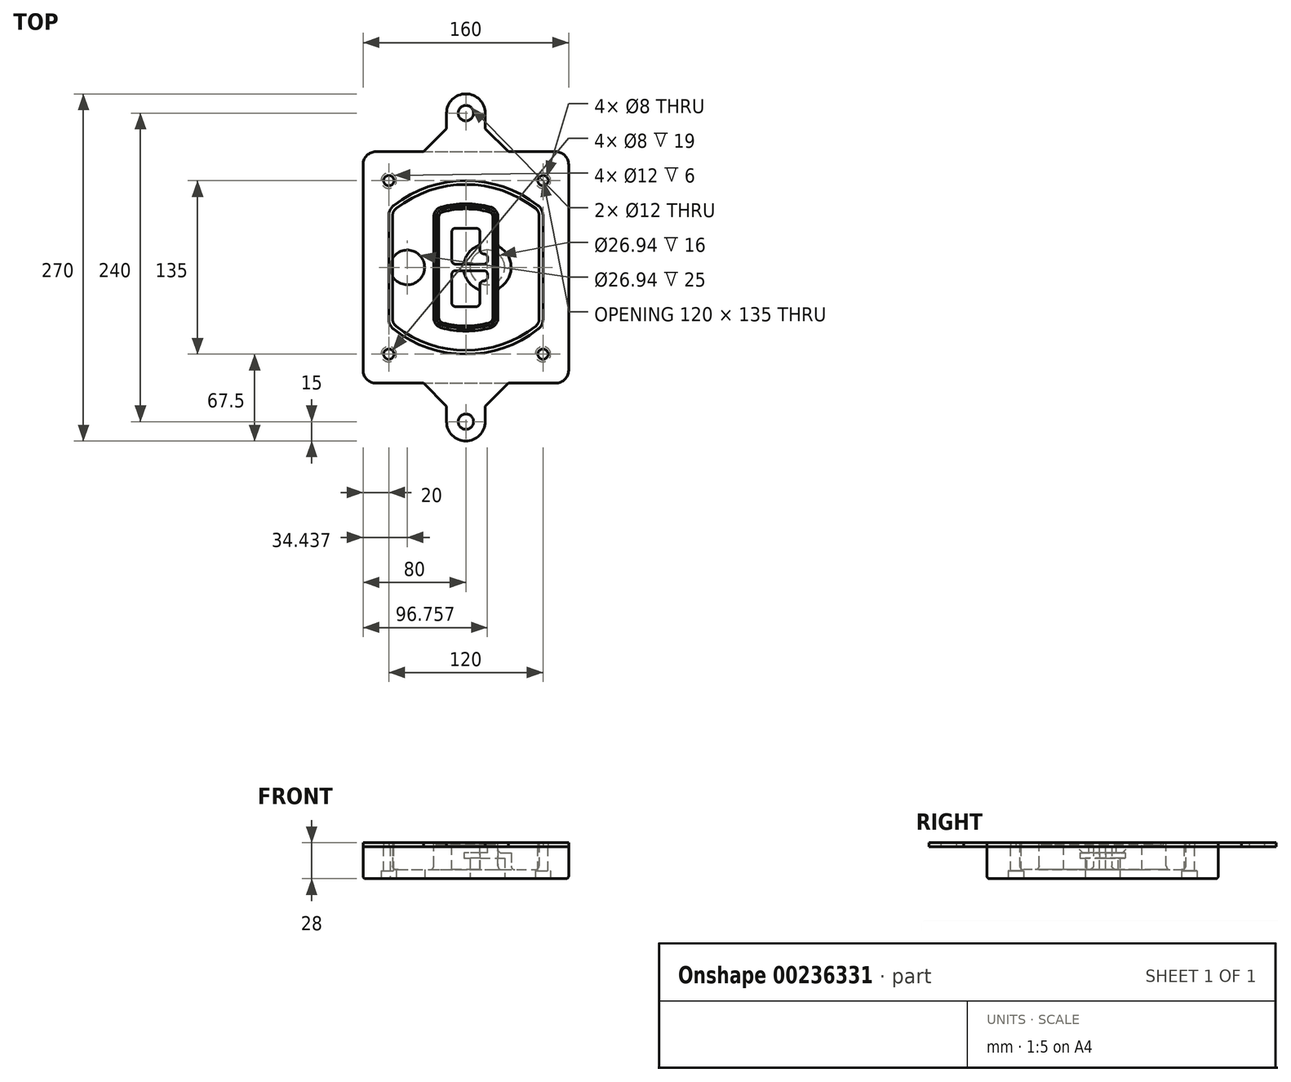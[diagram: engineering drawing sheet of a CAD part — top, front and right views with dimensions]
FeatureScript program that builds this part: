
annotation { "Feature Type Name" : "Feature", "Feature Type Description" : "" }
export const myFeature = defineFeature(function(context is Context, id is Id, definition is map)
    precondition{}
    {
        {
            var Q0;
            Q0=qCreatedBy(makeId("Top.planeOp"),FACE);
            var sketch = newSketch(context, id + "F0", { "sketchPlane" : qUnion([Q0])});
            skPoint(sketch, "E0.rect.middle", {"position": v(0, 0) * mm});
            skLineSegment(sketch, "E1.bottom", {"start": v(-70, -90) * mm, "end": v(70, -90) * mm});
            skLineSegment(sketch, "E1.top", {"start": v(-70, 90) * mm, "end": v(70, 90) * mm});
            skLineSegment(sketch, "E1.left", {"start": v(-80, -80) * mm, "end": v(-80, 80) * mm});
            skLineSegment(sketch, "E1.right", {"start": v(80, -80) * mm, "end": v(80, 80) * mm});
            skLineSegment(sketch, "E2", {"start": v(-80, 90) * mm, "end": v(80, -90) * mm, "construction": true});
            skLineSegment(sketch, "E3", {"start": v(80, 90) * mm, "end": v(-80, -90) * mm, "construction": true});
            skCircle(sketch, "E4", {"center": v(-60, 67.5) * mm, "radius": 4 * mm});
            skCircle(sketch, "E5", {"center": v(60, 67.5) * mm, "radius": 4 * mm});
            skCircle(sketch, "E6", {"center": v(60, -67.5) * mm, "radius": 4 * mm});
            skCircle(sketch, "E7", {"center": v(-60, -67.5) * mm, "radius": 4 * mm});
            skLineSegment(sketch, "E8", {"start": v(-60, 67.5) * mm, "end": v(60, 67.5) * mm, "construction": true});
            skLineSegment(sketch, "E9", {"start": v(60, 67.5) * mm, "end": v(60, -67.5) * mm, "construction": true});
            skLineSegment(sketch, "E10", {"start": v(60, -67.5) * mm, "end": v(-60, -67.5) * mm, "construction": true});
            skLineSegment(sketch, "E11", {"start": v(-60, -67.5) * mm, "end": v(-60, 67.5) * mm, "construction": true});
            skLineSegment(sketch, "E12", {"start": v(-60, 40.3) * mm, "end": v(-60, -40.3) * mm});
            skLineSegment(sketch, "E13", {"start": v(60, 40.3) * mm, "end": v(60, -40.3) * mm});
            skArc(sketch, "E14", {"start": v(56.15, 48.18) * mm, "mid": v(0, 67.5) * mm, "end": v(-56.15, 48.18) * mm});
            skArc(sketch, "E15", {"start": v(-56.15, -48.18) * mm, "mid": v(0, -67.5) * mm, "end": v(56.15, -48.18) * mm});
            skLineSegment(sketch, "E16", {"start": v(-60, 0) * mm, "end": v(60, 0) * mm, "construction": true});
            skPoint(sketch, "E17.visualSharp", {"position": v(-60, -45) * mm});
            skArc(sketch, "E17.filletArc", {"start": v(-60, -40.3) * mm, "mid": v(-58.99, -44.68) * mm, "end": v(-56.15, -48.18) * mm});
            skPoint(sketch, "E18.visualSharp", {"position": v(-60, 45) * mm});
            skArc(sketch, "E18.filletArc", {"start": v(-56.15, 48.18) * mm, "mid": v(-58.99, 44.68) * mm, "end": v(-60, 40.3) * mm});
            skPoint(sketch, "E19.visualSharp", {"position": v(60, 45) * mm});
            skArc(sketch, "E19.filletArc", {"start": v(60, 40.3) * mm, "mid": v(58.99, 44.68) * mm, "end": v(56.15, 48.18) * mm});
            skPoint(sketch, "E20.visualSharp", {"position": v(60, -45) * mm});
            skArc(sketch, "E20.filletArc", {"start": v(56.15, -48.18) * mm, "mid": v(58.99, -44.68) * mm, "end": v(60, -40.3) * mm});
            skPoint(sketch, "E21.visualSharp", {"position": v(-80, 90) * mm});
            skArc(sketch, "E21.filletArc", {"start": v(-70, 90) * mm, "mid": v(-77.07, 87.07) * mm, "end": v(-80, 80) * mm});
            skPoint(sketch, "E22.visualSharp", {"position": v(80, 90) * mm});
            skArc(sketch, "E22.filletArc", {"start": v(80, 80) * mm, "mid": v(77.07, 87.07) * mm, "end": v(70, 90) * mm});
            skPoint(sketch, "E23.visualSharp", {"position": v(80, -90) * mm});
            skArc(sketch, "E23.filletArc", {"start": v(70, -90) * mm, "mid": v(77.07, -87.07) * mm, "end": v(80, -80) * mm});
            skPoint(sketch, "E24.visualSharp", {"position": v(-80, -90) * mm});
            skArc(sketch, "E24.filletArc", {"start": v(-80, -80) * mm, "mid": v(-77.07, -87.07) * mm, "end": v(-70, -90) * mm});
            skArc(sketch, "E25.0", {"start": v(57, 40.3) * mm, "mid": v(56.3, 43.36) * mm, "end": v(54.3, 45.81) * mm});
            skLineSegment(sketch, "E25.1", {"start": v(57, 40.3) * mm, "end": v(57, -40.3) * mm});
            skArc(sketch, "E25.2", {"start": v(54.3, -45.81) * mm, "mid": v(56.3, -43.36) * mm, "end": v(57, -40.3) * mm});
            skArc(sketch, "E25.3", {"start": v(-54.3, -45.81) * mm, "mid": v(0, -64.5) * mm, "end": v(54.3, -45.81) * mm});
            skArc(sketch, "E25.4", {"start": v(-57, -40.3) * mm, "mid": v(-56.3, -43.36) * mm, "end": v(-54.3, -45.81) * mm});
            skArc(sketch, "E25.5", {"start": v(54.3, 45.81) * mm, "mid": v(0, 64.5) * mm, "end": v(-54.3, 45.81) * mm});
            skLineSegment(sketch, "E25.6", {"start": v(-57, 40.3) * mm, "end": v(-57, -40.3) * mm});
            skArc(sketch, "E25.7", {"start": v(-54.3, 45.81) * mm, "mid": v(-56.3, 43.36) * mm, "end": v(-57, 40.3) * mm});
            skArc(sketch, "E26.0", {"start": v(-58.62, 51.33) * mm, "mid": v(-62.58, 46.43) * mm, "end": v(-64, 40.3) * mm});
            skArc(sketch, "E26.1", {"start": v(58.62, 51.33) * mm, "mid": v(0, 71.5) * mm, "end": v(-58.62, 51.33) * mm});
            skArc(sketch, "E26.2", {"start": v(64, 40.3) * mm, "mid": v(62.58, 46.43) * mm, "end": v(58.62, 51.33) * mm});
            skLineSegment(sketch, "E26.3", {"start": v(64, 40.3) * mm, "end": v(64, -40.3) * mm});
            skArc(sketch, "E26.4", {"start": v(58.62, -51.33) * mm, "mid": v(62.58, -46.43) * mm, "end": v(64, -40.3) * mm});
            skLineSegment(sketch, "E26.5", {"start": v(-64, 40.3) * mm, "end": v(-64, -40.3) * mm});
            skArc(sketch, "E26.6", {"start": v(-58.62, -51.33) * mm, "mid": v(0, -71.5) * mm, "end": v(58.62, -51.33) * mm});
            skArc(sketch, "E26.7", {"start": v(-64, -40.3) * mm, "mid": v(-62.58, -46.43) * mm, "end": v(-58.62, -51.33) * mm});
            skSolve(sketch);
        }
        {
            var Q0;
            Q0=makeQuery(id+"F0.imprint","IMPRINT",FACE,{"disambiguationData":[TD([[makeQuery(id+"F0.imprint","IMPRINT",EDGE,{"derivedFrom":sQuery(id+"F0.wireOp",EDGE,"E1.bottom")}),1.0]])]});
            var Q1;
            Q1=makeQuery(id+"F0.imprint","IMPRINT",FACE,{"disambiguationData":[TD([[makeQuery(id+"F0.imprint","IMPRINT",EDGE,{"derivedFrom":sQuery(id+"F0.wireOp",EDGE,"E12")}),1.0]])]});
            var Q2;
            Q2=makeQuery(id+"F0.imprint","IMPRINT",FACE,{"disambiguationData":[TD([[makeQuery(id+"F0.imprint","IMPRINT",EDGE,{"derivedFrom":sQuery(id+"F0.wireOp",EDGE,"E25.0")}),1.0]])]});
            var Q3;
            Q3=makeQuery(id+"F0.imprint","IMPRINT",FACE,{"disambiguationData":[TD([[makeQuery(id+"F0.imprint","IMPRINT",EDGE,{"derivedFrom":sQuery(id+"F0.wireOp",EDGE,"E12")}),-1.0]])]});
            extrude(context, id + "F1", {"entities" : qUnion([Q0, Q1, Q2, Q3]), "oppositeDirection" : true, "depth" : 25 * mm});
        }
        {
            var Q0;
            Q0=makeQuery(id+"F0.imprint","IMPRINT",FACE,{"disambiguationData":[TD([[makeQuery(id+"F0.imprint","IMPRINT",EDGE,{"derivedFrom":sQuery(id+"F0.wireOp",EDGE,"E12")}),1.0]])]});
            extrude(context, id + "F2", {"entities" : qUnion([Q0]), "operationType" : NewBodyOperationType.ADD, "depth" : 3 * mm});
        }
        {
            var Q0;
            Q0=makeQuery(id+"F0.imprint","IMPRINT",FACE,{"disambiguationData":[TD([[makeQuery(id+"F0.imprint","IMPRINT",EDGE,{"derivedFrom":sQuery(id+"F0.wireOp",EDGE,"E25.0")}),1.0]])]});
            extrude(context, id + "F3", {"entities" : qUnion([Q0]), "operationType" : NewBodyOperationType.REMOVE, "oppositeDirection" : true, "depth" : 18 * mm});
        }
        {
            var Q0;
            Q0=makeQuery(id+"F2.opExtrude","CAP_FACE",FACE,{"disambiguationData":[OSD([sQuery(id+"F0.wireOp",EDGE,"E12"),sQuery(id+"F0.wireOp",EDGE,"E13"),sQuery(id+"F0.wireOp",EDGE,"E14"),sQuery(id+"F0.wireOp",EDGE,"E15"),sQuery(id+"F0.wireOp",EDGE,"E17.filletArc"),sQuery(id+"F0.wireOp",EDGE,"E18.filletArc"),sQuery(id+"F0.wireOp",EDGE,"E19.filletArc"),sQuery(id+"F0.wireOp",EDGE,"E20.filletArc"),sQuery(id+"F0.wireOp",EDGE,"E25.0"),sQuery(id+"F0.wireOp",EDGE,"E25.1"),sQuery(id+"F0.wireOp",EDGE,"E25.2"),sQuery(id+"F0.wireOp",EDGE,"E25.3"),sQuery(id+"F0.wireOp",EDGE,"E25.4"),sQuery(id+"F0.wireOp",EDGE,"E25.5"),sQuery(id+"F0.wireOp",EDGE,"E25.6"),sQuery(id+"F0.wireOp",EDGE,"E25.7")])],"isStart":false});
            var sketch = newSketch(context, id + "F4", { "sketchPlane" : qUnion([Q0])});
            skArc(sketch, "E27.0", {"start": v(-19.08, -46.97) * mm, "mid": v(0, -49.5) * mm, "end": v(19.08, -46.97) * mm});
            skArc(sketch, "E28.0", {"start": v(19.08, 46.97) * mm, "mid": v(0, 49.5) * mm, "end": v(-19.08, 46.97) * mm});
            skLineSegment(sketch, "E29", {"start": v(-25, 39.25) * mm, "end": v(-25, -39.25) * mm});
            skLineSegment(sketch, "E30", {"start": v(25, 39.25) * mm, "end": v(25, -39.25) * mm});
            skLineSegment(sketch, "E31", {"start": v(-25, 45.1) * mm, "end": v(25, 45.1) * mm, "construction": true});
            skLineSegment(sketch, "E32", {"start": v(-25, -45.1) * mm, "end": v(25, -45.1) * mm, "construction": true});
            skPoint(sketch, "E33.visualSharp", {"position": v(-25, 45.1) * mm});
            skArc(sketch, "E33.filletArc", {"start": v(-19.08, 46.97) * mm, "mid": v(-23.35, 44.11) * mm, "end": v(-25, 39.25) * mm});
            skPoint(sketch, "E34.visualSharp", {"position": v(25, 45.1) * mm});
            skArc(sketch, "E34.filletArc", {"start": v(25, 39.25) * mm, "mid": v(23.35, 44.11) * mm, "end": v(19.08, 46.97) * mm});
            skPoint(sketch, "E35.visualSharp", {"position": v(25, -45.1) * mm});
            skArc(sketch, "E35.filletArc", {"start": v(19.08, -46.97) * mm, "mid": v(23.35, -44.11) * mm, "end": v(25, -39.25) * mm});
            skPoint(sketch, "E36.visualSharp", {"position": v(-25, -45.1) * mm});
            skArc(sketch, "E36.filletArc", {"start": v(-25, -39.25) * mm, "mid": v(-23.35, -44.11) * mm, "end": v(-19.08, -46.97) * mm});
            skArc(sketch, "E37.0", {"start": v(54.3, 45.81) * mm, "mid": v(0, 64.5) * mm, "end": v(-54.3, 45.81) * mm});
            skArc(sketch, "E37.1", {"start": v(-54.3, 45.81) * mm, "mid": v(-56.3, 43.36) * mm, "end": v(-57, 40.3) * mm});
            skLineSegment(sketch, "E37.2", {"start": v(-57, 40.3) * mm, "end": v(-57, -40.3) * mm});
            skArc(sketch, "E37.3", {"start": v(-57, -40.3) * mm, "mid": v(-56.3, -43.36) * mm, "end": v(-54.3, -45.81) * mm});
            skArc(sketch, "E37.4", {"start": v(-54.3, -45.81) * mm, "mid": v(0, -64.5) * mm, "end": v(54.3, -45.81) * mm});
            skArc(sketch, "E37.5", {"start": v(54.3, -45.81) * mm, "mid": v(56.3, -43.36) * mm, "end": v(57, -40.3) * mm});
            skLineSegment(sketch, "E37.6", {"start": v(57, 40.3) * mm, "end": v(57, -40.3) * mm});
            skArc(sketch, "E37.7", {"start": v(57, 40.3) * mm, "mid": v(56.3, 43.36) * mm, "end": v(54.3, 45.81) * mm});
            skLineSegment(sketch, "E38.0", {"start": v(23, 39.25) * mm, "end": v(23, -39.25) * mm});
            skArc(sketch, "E38.1", {"start": v(18.56, -45.04) * mm, "mid": v(21.76, -42.9) * mm, "end": v(23, -39.25) * mm});
            skArc(sketch, "E38.2", {"start": v(-18.56, -45.04) * mm, "mid": v(0, -47.5) * mm, "end": v(18.56, -45.04) * mm});
            skArc(sketch, "E38.3", {"start": v(-23, -39.25) * mm, "mid": v(-21.76, -42.9) * mm, "end": v(-18.56, -45.04) * mm});
            skLineSegment(sketch, "E38.4", {"start": v(-23, 39.25) * mm, "end": v(-23, -39.25) * mm});
            skArc(sketch, "E38.5", {"start": v(23, 39.25) * mm, "mid": v(21.76, 42.9) * mm, "end": v(18.56, 45.04) * mm});
            skArc(sketch, "E38.6", {"start": v(-18.56, 45.04) * mm, "mid": v(-21.76, 42.9) * mm, "end": v(-23, 39.25) * mm});
            skArc(sketch, "E38.7", {"start": v(18.56, 45.04) * mm, "mid": v(0, 47.5) * mm, "end": v(-18.56, 45.04) * mm});
            skArc(sketch, "E39.0", {"start": v(21, 39.25) * mm, "mid": v(20.18, 41.68) * mm, "end": v(18.04, 43.1) * mm});
            skLineSegment(sketch, "E39.1", {"start": v(21, 39.25) * mm, "end": v(21, -39.25) * mm});
            skArc(sketch, "E39.2", {"start": v(18.04, -43.1) * mm, "mid": v(20.18, -41.68) * mm, "end": v(21, -39.25) * mm});
            skArc(sketch, "E39.3", {"start": v(-18.04, -43.1) * mm, "mid": v(0, -45.5) * mm, "end": v(18.04, -43.1) * mm});
            skArc(sketch, "E39.4", {"start": v(-21, -39.25) * mm, "mid": v(-20.18, -41.68) * mm, "end": v(-18.04, -43.1) * mm});
            skArc(sketch, "E39.5", {"start": v(18.04, 43.1) * mm, "mid": v(0, 45.5) * mm, "end": v(-18.04, 43.1) * mm});
            skLineSegment(sketch, "E39.6", {"start": v(-21, 39.25) * mm, "end": v(-21, -39.25) * mm});
            skArc(sketch, "E39.7", {"start": v(-18.04, 43.1) * mm, "mid": v(-20.18, 41.68) * mm, "end": v(-21, 39.25) * mm});
            skLineSegment(sketch, "E40", {"start": v(-25, 0) * mm, "end": v(25, 0) * mm, "construction": true});
            skLineSegment(sketch, "E41", {"start": v(-11, 5.5) * mm, "end": v(-11, 27.5) * mm});
            skLineSegment(sketch, "E42", {"start": v(-8, 30.5) * mm, "end": v(8, 30.5) * mm});
            skLineSegment(sketch, "E43", {"start": v(11, 27.5) * mm, "end": v(11, 13.5) * mm});
            skLineSegment(sketch, "E44", {"start": v(14, 10.5) * mm, "end": v(14, 10.5) * mm});
            skLineSegment(sketch, "E45", {"start": v(17, 7.5) * mm, "end": v(17, 5.5) * mm});
            skLineSegment(sketch, "E46", {"start": v(14, 2.5) * mm, "end": v(-8, 2.5) * mm});
            skPoint(sketch, "E47.visualSharp", {"position": v(-11, 30.5) * mm});
            skArc(sketch, "E47.filletArc", {"start": v(-8, 30.5) * mm, "mid": v(-10.12, 29.62) * mm, "end": v(-11, 27.5) * mm});
            skPoint(sketch, "E48.visualSharp", {"position": v(11, 30.5) * mm});
            skArc(sketch, "E48.filletArc", {"start": v(11, 27.5) * mm, "mid": v(10.12, 29.62) * mm, "end": v(8, 30.5) * mm});
            skPoint(sketch, "E49.visualSharp", {"position": v(11, 10.5) * mm});
            skArc(sketch, "E49.filletArc", {"start": v(11, 13.5) * mm, "mid": v(11.88, 11.38) * mm, "end": v(14, 10.5) * mm});
            skPoint(sketch, "E50.visualSharp", {"position": v(17, 10.5) * mm});
            skArc(sketch, "E50.filletArc", {"start": v(17, 7.5) * mm, "mid": v(16.12, 9.62) * mm, "end": v(14, 10.5) * mm});
            skPoint(sketch, "E51.visualSharp", {"position": v(17, 2.5) * mm});
            skArc(sketch, "E51.filletArc", {"start": v(14, 2.5) * mm, "mid": v(16.12, 3.38) * mm, "end": v(17, 5.5) * mm});
            skPoint(sketch, "E52.visualSharp", {"position": v(-11, 2.5) * mm});
            skArc(sketch, "E52.filletArc", {"start": v(-11, 5.5) * mm, "mid": v(-10.12, 3.38) * mm, "end": v(-8, 2.5) * mm});
            skLineSegment(sketch, "E53.0.MirrorCS", {"start": v(14, -2.5) * mm, "end": v(-8, -2.5) * mm});
            skArc(sketch, "E54.0.MirrorCS", {"start": v(-11, -5.5) * mm, "mid": v(-10.12, -3.38) * mm, "end": v(-8, -2.5) * mm});
            skLineSegment(sketch, "E55.0.MirrorCS", {"start": v(-11, -5.5) * mm, "end": v(-11, -27.5) * mm});
            skArc(sketch, "E56.0.MirrorCS", {"start": v(-8, -30.5) * mm, "mid": v(-10.12, -29.62) * mm, "end": v(-11, -27.5) * mm});
            skLineSegment(sketch, "E57.0.MirrorCS", {"start": v(-8, -30.5) * mm, "end": v(8, -30.5) * mm});
            skArc(sketch, "E58.0.MirrorCS", {"start": v(11, -27.5) * mm, "mid": v(10.12, -29.62) * mm, "end": v(8, -30.5) * mm});
            skLineSegment(sketch, "E59.0.MirrorCS", {"start": v(11, -27.5) * mm, "end": v(11, -13.5) * mm});
            skArc(sketch, "E60.0.MirrorCS", {"start": v(11, -13.5) * mm, "mid": v(11.88, -11.38) * mm, "end": v(14, -10.5) * mm});
            skArc(sketch, "E61.0.MirrorCS", {"start": v(17, -7.5) * mm, "mid": v(16.12, -9.62) * mm, "end": v(14, -10.5) * mm});
            skLineSegment(sketch, "E62.0.MirrorCS", {"start": v(17, -7.5) * mm, "end": v(17, -5.5) * mm});
            skArc(sketch, "E63.0.MirrorCS", {"start": v(14, -2.5) * mm, "mid": v(16.12, -3.38) * mm, "end": v(17, -5.5) * mm});
            skSolve(sketch);
        }
        {
            var Q0;
            Q0=makeQuery(id+"F4.imprint","IMPRINT",FACE,{"disambiguationData":[TD([[makeQuery(id+"F4.imprint","IMPRINT",EDGE,{"derivedFrom":sQuery(id+"F4.wireOp",EDGE,"E27.0")}),1.0]])]});
            var Q1;
            Q1=makeQuery(id+"F4.imprint","IMPRINT",FACE,{"disambiguationData":[TD([[makeQuery(id+"F4.imprint","IMPRINT",EDGE,{"derivedFrom":sQuery(id+"F4.wireOp",EDGE,"E38.0")}),-1.0]])]});
            var Q2;
            Q2=makeQuery(id+"F4.imprint","IMPRINT",FACE,{"disambiguationData":[TD([[makeQuery(id+"F4.imprint","IMPRINT",EDGE,{"derivedFrom":sQuery(id+"F4.wireOp",EDGE,"E39.0")}),1.0]])]});
            extrude(context, id + "F5", {"entities" : qUnion([Q0, Q1, Q2]), "operationType" : NewBodyOperationType.ADD, "endBound" : BoundingType.UP_TO_NEXT, "oppositeDirection" : true, "depth" : 25 * mm});
        }
        {
            var Q0;
            Q0=makeQuery(id+"F4.imprint","IMPRINT",FACE,{"disambiguationData":[TD([[makeQuery(id+"F4.imprint","IMPRINT",EDGE,{"derivedFrom":sQuery(id+"F4.wireOp",EDGE,"E38.0")}),-1.0]])]});
            extrude(context, id + "F6", {"entities" : qUnion([Q0]), "operationType" : NewBodyOperationType.REMOVE, "oppositeDirection" : true, "depth" : 2 * mm});
        }
        {
            var Q0;
            Q0=makeQuery(id+"F1.opExtrude","CAP_FACE",FACE,{"disambiguationData":[OSD([sQuery(id+"F0.wireOp",EDGE,"E1.bottom"),sQuery(id+"F0.wireOp",EDGE,"E1.top"),sQuery(id+"F0.wireOp",EDGE,"E1.left"),sQuery(id+"F0.wireOp",EDGE,"E1.right"),sQuery(id+"F0.wireOp",EDGE,"E4"),sQuery(id+"F0.wireOp",EDGE,"E5"),sQuery(id+"F0.wireOp",EDGE,"E6"),sQuery(id+"F0.wireOp",EDGE,"E7"),sQuery(id+"F0.wireOp",EDGE,"E21.filletArc"),sQuery(id+"F0.wireOp",EDGE,"E22.filletArc"),sQuery(id+"F0.wireOp",EDGE,"E23.filletArc"),sQuery(id+"F0.wireOp",EDGE,"E24.filletArc")])],"isStart":false});
            var sketch = newSketch(context, id + "F7", { "sketchPlane" : qUnion([Q0])});
            skCircle(sketch, "E64", {"center": v(16.76, 0) * mm, "radius": 13.47 * mm});
            skCircle(sketch, "E65", {"center": v(-45.56, 0) * mm, "radius": 13.47 * mm});
            skLineSegment(sketch, "E66", {"start": v(80, 0) * mm, "end": v(-80, 0) * mm});
            skCircle(sketch, "E67", {"center": v(16.76, 0) * mm, "radius": 18.47 * mm});
            skCircle(sketch, "E68", {"center": v(60, -67.5) * mm, "radius": 6 * mm});
            skCircle(sketch, "E69", {"center": v(-60, -67.5) * mm, "radius": 6 * mm});
            skCircle(sketch, "E70", {"center": v(-60, 67.5) * mm, "radius": 6 * mm});
            skCircle(sketch, "E71", {"center": v(60, 67.5) * mm, "radius": 6 * mm});
            skSolve(sketch);
        }
        {
            var Q0;
            {var subQ1=sQuery(id+"F7.wireOp",EDGE,"E66");var subQ4=sQuery(id+"F7.wireOp",EDGE,"E64");var subQ6=makeQuery(id+"F7.imprint","INTERSECT",VERTEX,{"disambiguationData":[OD(0.0)],"derivedFrom":[subQ4,subQ1]});Q0=makeQuery(id+"F7.imprint","IMPRINT",FACE,{"disambiguationData":[TD([[makeQuery(id+"F7.imprint","IMPRINT",EDGE,{"disambiguationData":[TD([[subQ6,-1.0]])],"derivedFrom":subQ4}),-1.0]])]});}
            var Q1;
            {var subQ0=sQuery(id+"F7.wireOp",EDGE,"E66");var subQ1=sQuery(id+"F7.wireOp",EDGE,"E64");var subQ3=makeQuery(id+"F7.imprint","INTERSECT",VERTEX,{"disambiguationData":[OD(0.0)],"derivedFrom":[subQ1,subQ0]});Q1=makeQuery(id+"F7.imprint","IMPRINT",FACE,{"disambiguationData":[TD([[makeQuery(id+"F7.imprint","IMPRINT",EDGE,{"disambiguationData":[TD([[subQ3,-1.0]])],"derivedFrom":subQ1}),1.0]])]});}
            var Q2;
            {var subQ0=sQuery(id+"F7.wireOp",EDGE,"E66");var subQ1=sQuery(id+"F7.wireOp",EDGE,"E64");var subQ3=makeQuery(id+"F7.imprint","INTERSECT",VERTEX,{"disambiguationData":[OD(0.0)],"derivedFrom":[subQ1,subQ0]});Q2=makeQuery(id+"F7.imprint","IMPRINT",FACE,{"disambiguationData":[TD([[makeQuery(id+"F7.imprint","IMPRINT",EDGE,{"disambiguationData":[TD([[subQ3,1.0]])],"derivedFrom":subQ1}),1.0]])]});}
            var Q3;
            {var subQ1=sQuery(id+"F7.wireOp",EDGE,"E66");var subQ4=sQuery(id+"F7.wireOp",EDGE,"E64");var subQ6=makeQuery(id+"F7.imprint","INTERSECT",VERTEX,{"disambiguationData":[OD(0.0)],"derivedFrom":[subQ4,subQ1]});Q3=makeQuery(id+"F7.imprint","IMPRINT",FACE,{"disambiguationData":[TD([[makeQuery(id+"F7.imprint","IMPRINT",EDGE,{"disambiguationData":[TD([[subQ6,1.0]])],"derivedFrom":subQ4}),-1.0]])]});}
            extrude(context, id + "F8", {"entities" : qUnion([Q0, Q1, Q2, Q3]), "operationType" : NewBodyOperationType.ADD, "oppositeDirection" : true, "depth" : 20 * mm});
        }
        {
            var Q0;
            {var subQ0=sQuery(id+"F7.wireOp",EDGE,"E66");var subQ1=sQuery(id+"F7.wireOp",EDGE,"E64");var subQ3=makeQuery(id+"F7.imprint","INTERSECT",VERTEX,{"disambiguationData":[OD(0.0)],"derivedFrom":[subQ1,subQ0]});Q0=makeQuery(id+"F7.imprint","IMPRINT",FACE,{"disambiguationData":[TD([[makeQuery(id+"F7.imprint","IMPRINT",EDGE,{"disambiguationData":[TD([[subQ3,-1.0]])],"derivedFrom":subQ1}),1.0]])]});}
            var Q1;
            {var subQ0=sQuery(id+"F7.wireOp",EDGE,"E66");var subQ1=sQuery(id+"F7.wireOp",EDGE,"E64");var subQ3=makeQuery(id+"F7.imprint","INTERSECT",VERTEX,{"disambiguationData":[OD(0.0)],"derivedFrom":[subQ1,subQ0]});Q1=makeQuery(id+"F7.imprint","IMPRINT",FACE,{"disambiguationData":[TD([[makeQuery(id+"F7.imprint","IMPRINT",EDGE,{"disambiguationData":[TD([[subQ3,1.0]])],"derivedFrom":subQ1}),1.0]])]});}
            extrude(context, id + "F9", {"entities" : qUnion([Q0, Q1]), "operationType" : NewBodyOperationType.REMOVE, "oppositeDirection" : true, "depth" : 16 * mm});
        }
        {
            var Q0;
            {var subQ0=sQuery(id+"F7.wireOp",EDGE,"E66");var subQ1=sQuery(id+"F7.wireOp",EDGE,"E65");var subQ3=makeQuery(id+"F7.imprint","INTERSECT",VERTEX,{"disambiguationData":[OD(0.0)],"derivedFrom":[subQ1,subQ0]});Q0=makeQuery(id+"F7.imprint","IMPRINT",FACE,{"disambiguationData":[TD([[makeQuery(id+"F7.imprint","IMPRINT",EDGE,{"disambiguationData":[TD([[subQ3,-1.0]])],"derivedFrom":subQ1}),1.0]])]});}
            var Q1;
            {var subQ0=sQuery(id+"F7.wireOp",EDGE,"E66");var subQ1=sQuery(id+"F7.wireOp",EDGE,"E65");var subQ3=makeQuery(id+"F7.imprint","INTERSECT",VERTEX,{"disambiguationData":[OD(0.0)],"derivedFrom":[subQ1,subQ0]});Q1=makeQuery(id+"F7.imprint","IMPRINT",FACE,{"disambiguationData":[TD([[makeQuery(id+"F7.imprint","IMPRINT",EDGE,{"disambiguationData":[TD([[subQ3,1.0]])],"derivedFrom":subQ1}),1.0]])]});}
            extrude(context, id + "F10", {"entities" : qUnion([Q0, Q1]), "operationType" : NewBodyOperationType.REMOVE, "oppositeDirection" : true, "depth" : 25 * mm});
        }
        {
            var Q0;
            Q0=makeQuery(id+"F7.imprint","IMPRINT",FACE,{"disambiguationData":[TD([[makeQuery(id+"F7.imprint","IMPRINT",EDGE,{"derivedFrom":sQuery(id+"F7.wireOp",EDGE,"E68")}),1.0]])]});
            var Q1;
            Q1=makeQuery(id+"F7.imprint","IMPRINT",FACE,{"disambiguationData":[TD([[makeQuery(id+"F7.imprint","IMPRINT",EDGE,{"derivedFrom":makeQuery(id+"F1.opExtrude","CAP_EDGE",EDGE,{"disambiguationData":[OSD([sQuery(id+"F0.wireOp",EDGE,"E5")])],"isStart":false})}),-1.0]])]});
            var Q2;
            Q2=makeQuery(id+"F7.imprint","IMPRINT",FACE,{"disambiguationData":[TD([[makeQuery(id+"F7.imprint","IMPRINT",EDGE,{"derivedFrom":sQuery(id+"F7.wireOp",EDGE,"E69")}),1.0]])]});
            var Q3;
            Q3=makeQuery(id+"F7.imprint","IMPRINT",FACE,{"disambiguationData":[TD([[makeQuery(id+"F7.imprint","IMPRINT",EDGE,{"derivedFrom":makeQuery(id+"F1.opExtrude","CAP_EDGE",EDGE,{"disambiguationData":[OSD([sQuery(id+"F0.wireOp",EDGE,"E4")])],"isStart":false})}),-1.0]])]});
            var Q4;
            Q4=makeQuery(id+"F7.imprint","IMPRINT",FACE,{"disambiguationData":[TD([[makeQuery(id+"F7.imprint","IMPRINT",EDGE,{"derivedFrom":sQuery(id+"F7.wireOp",EDGE,"E70")}),1.0]])]});
            var Q5;
            Q5=makeQuery(id+"F7.imprint","IMPRINT",FACE,{"disambiguationData":[TD([[makeQuery(id+"F7.imprint","IMPRINT",EDGE,{"derivedFrom":makeQuery(id+"F1.opExtrude","CAP_EDGE",EDGE,{"disambiguationData":[OSD([sQuery(id+"F0.wireOp",EDGE,"E7")])],"isStart":false})}),-1.0]])]});
            var Q6;
            Q6=makeQuery(id+"F7.imprint","IMPRINT",FACE,{"disambiguationData":[TD([[makeQuery(id+"F7.imprint","IMPRINT",EDGE,{"derivedFrom":sQuery(id+"F7.wireOp",EDGE,"E71")}),1.0]])]});
            var Q7;
            Q7=makeQuery(id+"F7.imprint","IMPRINT",FACE,{"disambiguationData":[TD([[makeQuery(id+"F7.imprint","IMPRINT",EDGE,{"derivedFrom":makeQuery(id+"F1.opExtrude","CAP_EDGE",EDGE,{"disambiguationData":[OSD([sQuery(id+"F0.wireOp",EDGE,"E6")])],"isStart":false})}),-1.0]])]});
            extrude(context, id + "F11", {"entities" : qUnion([Q0, Q1, Q2, Q3, Q4, Q5, Q6, Q7]), "operationType" : NewBodyOperationType.REMOVE, "oppositeDirection" : true, "depth" : 6 * mm});
        }
        {
            var Q0;
            Q0=makeQuery(id+"F9.boolean.opBoolean","COPY",FACE,{"derivedFrom":makeQuery(id+"F9.opExtrude","CAP_FACE",FACE,{"disambiguationData":[OSD([sQuery(id+"F7.wireOp",EDGE,"E64")])],"isStart":false})});
            var sketch = newSketch(context, id + "F12", { "sketchPlane" : qUnion([Q0])});
            skArc(sketch, "E72.0", {"start": v(11, 17.55) * mm, "mid": v(2.57, 11.82) * mm, "end": v(-1.54, 2.5) * mm});
            skArc(sketch, "E72.1", {"start": v(-1.54, -2.5) * mm, "mid": v(2.57, -11.82) * mm, "end": v(11, -17.55) * mm});
            skLineSegment(sketch, "E73", {"start": v(-1.54, -2.5) * mm, "end": v(14, -2.5) * mm});
            skLineSegment(sketch, "E74.0", {"start": v(14, 2.5) * mm, "end": v(-1.54, 2.5) * mm});
            skArc(sketch, "E74.1", {"start": v(14, 2.5) * mm, "mid": v(16.12, 3.38) * mm, "end": v(17, 5.5) * mm});
            skLineSegment(sketch, "E74.2", {"start": v(17, 7.5) * mm, "end": v(17, 5.5) * mm});
            skArc(sketch, "E74.3", {"start": v(17, 7.5) * mm, "mid": v(16.12, 9.62) * mm, "end": v(14, 10.5) * mm});
            skArc(sketch, "E74.4", {"start": v(11, 13.5) * mm, "mid": v(11.88, 11.38) * mm, "end": v(14, 10.5) * mm});
            skLineSegment(sketch, "E74.5", {"start": v(11, 17.55) * mm, "end": v(11, 13.5) * mm});
            skLineSegment(sketch, "E74.7", {"start": v(14, -2.5) * mm, "end": v(-1.54, -2.5) * mm});
            skArc(sketch, "E74.8", {"start": v(14, -2.5) * mm, "mid": v(16.12, -3.38) * mm, "end": v(17, -5.5) * mm});
            skLineSegment(sketch, "E74.9", {"start": v(17, -7.5) * mm, "end": v(17, -5.5) * mm});
            skArc(sketch, "E74.10", {"start": v(17, -7.5) * mm, "mid": v(16.12, -9.62) * mm, "end": v(14, -10.5) * mm});
            skArc(sketch, "E74.11", {"start": v(11, -13.5) * mm, "mid": v(11.88, -11.38) * mm, "end": v(14, -10.5) * mm});
            skLineSegment(sketch, "E74.12", {"start": v(11, -17.55) * mm, "end": v(11, -13.5) * mm});
            skPoint(sketch, "E75.orphan", {"position": v(11, -27.5) * mm});
            skPoint(sketch, "E76.orphan", {"position": v(-8, -2.5) * mm});
            skPoint(sketch, "E77.orphan", {"position": v(-8, 2.5) * mm});
            skPoint(sketch, "E78.orphan", {"position": v(11, 27.5) * mm});
            skSolve(sketch);
        }
        {
            var Q0;
            {var subQ7=sQuery(id+"F12.wireOp",EDGE,"E72.0");var subQ14=sQuery(id+"F12.wireOp",EDGE,"E72.1");var subQ16=sQuery(id+"F12.wireOp",EDGE,"E74.1");var subQ18=sQuery(id+"F12.wireOp",EDGE,"E74.8");Q0=qUnion([makeQuery(id+"F12.imprint","IMPRINT",FACE,{"disambiguationData":[TD([[makeQuery(id+"F12.imprint","IMPRINT",EDGE,{"derivedFrom":subQ7}),1.0]])]}),makeQuery(id+"F12.imprint","IMPRINT",FACE,{"disambiguationData":[TD([[makeQuery(id+"F12.imprint","IMPRINT",EDGE,{"derivedFrom":subQ14}),1.0]])]}),makeQuery(id+"F12.imprint","IMPRINT",FACE,{"disambiguationData":[TD([[makeQuery(id+"F12.imprint","IMPRINT",EDGE,{"derivedFrom":subQ16}),1.0]])]}),makeQuery(id+"F12.imprint","IMPRINT",FACE,{"disambiguationData":[TD([[makeQuery(id+"F12.imprint","IMPRINT",EDGE,{"derivedFrom":subQ18}),-1.0]])]})]);}
            var Q1;
            Q1=makeQuery(id+"F5.boolean.opBoolean","SPLIT",FACE,{"disambiguationData":[TD([makeQuery(id+"F5.opExtrude","SWEPT_FACE",FACE,{"disambiguationData":[OSD([sQuery(id+"F4.wireOp",EDGE,"E41")])]})])],"derivedFrom":makeQuery(id+"F3.boolean.opBoolean","COPY",FACE,{"derivedFrom":makeQuery(id+"F3.opExtrude","CAP_FACE",FACE,{"disambiguationData":[OSD([sQuery(id+"F0.wireOp",EDGE,"E25.0"),sQuery(id+"F0.wireOp",EDGE,"E25.1"),sQuery(id+"F0.wireOp",EDGE,"E25.2"),sQuery(id+"F0.wireOp",EDGE,"E25.3"),sQuery(id+"F0.wireOp",EDGE,"E25.4"),sQuery(id+"F0.wireOp",EDGE,"E25.5"),sQuery(id+"F0.wireOp",EDGE,"E25.6"),sQuery(id+"F0.wireOp",EDGE,"E25.7")])],"isStart":false})})});
            extrude(context, id + "F13", {"entities" : qUnion([Q0]), "operationType" : NewBodyOperationType.REMOVE, "endBound" : BoundingType.UP_TO_SURFACE, "endBoundEntityFace" : qUnion([Q1]), "depth" : 25 * mm});
        }
        {
            var Q0;
            Q0=makeQuery(id+"F3.boolean.opBoolean","COPY",EDGE,{"derivedFrom":makeQuery(id+"F3.opExtrude","CAP_EDGE",EDGE,{"disambiguationData":[OSD([sQuery(id+"F0.wireOp",EDGE,"E25.6")])],"isStart":false})});
            var Q1;
            Q1=makeQuery(id+"F8.boolean.opBoolean","INTERSECT",EDGE,{"derivedFrom":[makeQuery(id+"F5.opExtrude","SWEPT_FACE",FACE,{"disambiguationData":[OSD([sQuery(id+"F4.wireOp",EDGE,"E30")])]}),makeQuery(id+"F8.opExtrude","CAP_FACE",FACE,{"disambiguationData":[OSD([sQuery(id+"F7.wireOp",EDGE,"E67")])],"isStart":false})]});
            var Q2;
            Q2=makeQuery(id+"F8.boolean.opBoolean","INTERSECT",EDGE,{"disambiguationData":[OD(1.0)],"derivedFrom":[makeQuery(id+"F5.opExtrude","SWEPT_FACE",FACE,{"disambiguationData":[OSD([sQuery(id+"F4.wireOp",EDGE,"E30")])]}),makeQuery(id+"F8.opExtrude","SWEPT_FACE",FACE,{"disambiguationData":[OSD([sQuery(id+"F7.wireOp",EDGE,"E67")])]})]});
            var Q3;
            {var subQ0=sQuery(id+"F4.wireOp",EDGE,"E30");Q3=makeQuery(id+"F8.boolean.opBoolean","SPLIT",EDGE,{"disambiguationData":[TD([makeQuery(id+"F5.opExtrude","SWEPT_FACE",FACE,{"disambiguationData":[OSD([sQuery(id+"F4.wireOp",EDGE,"E35.filletArc")])]})])],"derivedFrom":makeQuery(id+"F5.opExtrude","CAP_EDGE",EDGE,{"disambiguationData":[OSD([subQ0])],"isStart":false})});}
            var Q4;
            {var subQ0=sQuery(id+"F0.wireOp",EDGE,"E25.7");var subQ1=sQuery(id+"F0.wireOp",EDGE,"E25.1");var subQ2=sQuery(id+"F0.wireOp",EDGE,"E25.6");var subQ3=sQuery(id+"F0.wireOp",EDGE,"E25.5");var subQ4=sQuery(id+"F0.wireOp",EDGE,"E25.4");var subQ5=sQuery(id+"F0.wireOp",EDGE,"E25.0");var subQ6=sQuery(id+"F0.wireOp",EDGE,"E25.2");var subQ7=sQuery(id+"F0.wireOp",EDGE,"E25.3");Q4=makeQuery(id+"F8.boolean.opBoolean","INTERSECT",EDGE,{"derivedFrom":[makeQuery(id+"F5.boolean.opBoolean","SPLIT",FACE,{"disambiguationData":[TD([makeQuery(id+"F2.opExtrude","SWEPT_FACE",FACE,{"disambiguationData":[OSD([subQ5])]})])],"derivedFrom":makeQuery(id+"F3.boolean.opBoolean","COPY",FACE,{"derivedFrom":makeQuery(id+"F3.opExtrude","CAP_FACE",FACE,{"disambiguationData":[OSD([subQ5,subQ1,subQ6,subQ7,subQ4,subQ3,subQ2,subQ0])],"isStart":false})})}),makeQuery(id+"F8.opExtrude","SWEPT_FACE",FACE,{"disambiguationData":[OSD([sQuery(id+"F7.wireOp",EDGE,"E67")])]})]});}
            var Q5;
            Q5=makeQuery(id+"F8.boolean.opBoolean","INTERSECT",EDGE,{"disambiguationData":[OD(0.0)],"derivedFrom":[makeQuery(id+"F5.opExtrude","SWEPT_FACE",FACE,{"disambiguationData":[OSD([sQuery(id+"F4.wireOp",EDGE,"E30")])]}),makeQuery(id+"F8.opExtrude","SWEPT_FACE",FACE,{"disambiguationData":[OSD([sQuery(id+"F7.wireOp",EDGE,"E67")])]})]});
            fillet(context, id + "F14", {"entities" : qUnion([Q0, Q1, Q2, Q3, Q4, Q5]), "radius" : 3 * mm, "tangentPropagation" : true, "allowEdgeOverflow" : false});
        }
        {
            var Q0;
            Q0=makeQuery(id+"F1.opExtrude","CAP_EDGE",EDGE,{"disambiguationData":[OSD([sQuery(id+"F0.wireOp",EDGE,"E1.bottom")])],"isStart":false});
            fillet(context, id + "F15", {"entities" : qUnion([Q0]), "radius" : 2 * mm, "tangentPropagation" : true, "allowEdgeOverflow" : false});
        }
        {
            var Q0;
            {var subQ0=sQuery(id+"F0.wireOp",EDGE,"E22.filletArc");var subQ1=sQuery(id+"F0.wireOp",EDGE,"E7");var subQ2=sQuery(id+"F0.wireOp",EDGE,"E6");var subQ3=sQuery(id+"F0.wireOp",EDGE,"E5");var subQ4=sQuery(id+"F0.wireOp",EDGE,"E4");var subQ5=sQuery(id+"F0.wireOp",EDGE,"E1.bottom");var subQ6=sQuery(id+"F0.wireOp",EDGE,"E21.filletArc");var subQ7=sQuery(id+"F0.wireOp",EDGE,"E1.top");var subQ8=sQuery(id+"F0.wireOp",EDGE,"E1.left");var subQ9=sQuery(id+"F0.wireOp",EDGE,"E1.right");var subQ10=sQuery(id+"F0.wireOp",EDGE,"E23.filletArc");var subQ11=sQuery(id+"F0.wireOp",EDGE,"E24.filletArc");Q0=makeQuery(id+"F2.boolean.opBoolean","SPLIT",FACE,{"disambiguationData":[TD([makeQuery(id+"F1.opExtrude","SWEPT_FACE",FACE,{"disambiguationData":[OSD([subQ5])]})])],"derivedFrom":makeQuery(id+"F1.opExtrude","CAP_FACE",FACE,{"disambiguationData":[OSD([subQ5,subQ7,subQ8,subQ9,subQ4,subQ3,subQ2,subQ1,subQ6,subQ0,subQ10,subQ11])],"isStart":true})});}
            var sketch = newSketch(context, id + "F16", { "sketchPlane" : qUnion([Q0])});
            skLineSegment(sketch, "E79", {"start": v(0, 90) * mm, "end": v(0, 120) * mm, "construction": true});
            skPoint(sketch, "E79.endSnap0", {"position": v(0, 90) * mm});
            skCircle(sketch, "E80", {"center": v(0, 120) * mm, "radius": 6 * mm});
            skLineSegment(sketch, "E81", {"start": v(-33, 90) * mm, "end": v(-15, 108) * mm});
            skLineSegment(sketch, "E82", {"start": v(-15, 108) * mm, "end": v(-15, 120) * mm});
            skLineSegment(sketch, "E83", {"start": v(33, 90) * mm, "end": v(15, 108) * mm});
            skLineSegment(sketch, "E84", {"start": v(15, 108) * mm, "end": v(15, 120) * mm});
            skArc(sketch, "E85", {"start": v(15, 120) * mm, "mid": v(0, 135) * mm, "end": v(-15, 120) * mm});
            skLineSegment(sketch, "E86", {"start": v(-80, 0) * mm, "end": v(80, 0) * mm, "construction": true});
            skLineSegment(sketch, "E87.MirrorCS", {"start": v(-15, -108) * mm, "end": v(-15, -120) * mm});
            skLineSegment(sketch, "E88.MirrorCS", {"start": v(33, -90) * mm, "end": v(15, -108) * mm});
            skLineSegment(sketch, "E89.MirrorCS", {"start": v(0, -90) * mm, "end": v(0, -120) * mm, "construction": true});
            skCircle(sketch, "E90.MirrorC", {"center": v(0, -120) * mm, "radius": 6 * mm});
            skPoint(sketch, "E91.MirrorP", {"position": v(0, -90) * mm});
            skLineSegment(sketch, "E92.MirrorCS", {"start": v(-33, -90) * mm, "end": v(-15, -108) * mm});
            skLineSegment(sketch, "E93.MirrorCS", {"start": v(15, -108) * mm, "end": v(15, -120) * mm});
            skArc(sketch, "E94.MirrorCS", {"start": v(15, -120) * mm, "mid": v(0, -135) * mm, "end": v(-15, -120) * mm});
            skSolve(sketch);
        }
        {
            var Q0;
            {var subQ1=sQuery(id+"F16.wireOp",EDGE,"E81");Q0=makeQuery(id+"F16.imprint","IMPRINT",FACE,{"disambiguationData":[TD([[makeQuery(id+"F16.imprint","IMPRINT",EDGE,{"derivedFrom":subQ1}),-1.0]])]});}
            var Q1;
            Q1=makeQuery(id+"F16.imprint","IMPRINT",FACE,{"disambiguationData":[TD([[makeQuery(id+"F16.imprint","IMPRINT",EDGE,{"derivedFrom":makeQuery(id+"F1.opExtrude","CAP_EDGE",EDGE,{"disambiguationData":[OSD([sQuery(id+"F0.wireOp",EDGE,"E1.left")])],"isStart":true})}),-1.0]])]});
            var Q2;
            Q2=makeQuery(id+"F16.imprint","IMPRINT",FACE,{"disambiguationData":[TD([[makeQuery(id+"F16.imprint","IMPRINT",EDGE,{"derivedFrom":sQuery(id+"F16.wireOp",EDGE,"E87.MirrorCS")}),1.0]])]});
            var Q3;
            Q3=makeQuery(id+"F2.opExtrude","CAP_FACE",FACE,{"disambiguationData":[OSD([sQuery(id+"F0.wireOp",EDGE,"E12"),sQuery(id+"F0.wireOp",EDGE,"E13"),sQuery(id+"F0.wireOp",EDGE,"E14"),sQuery(id+"F0.wireOp",EDGE,"E15"),sQuery(id+"F0.wireOp",EDGE,"E17.filletArc"),sQuery(id+"F0.wireOp",EDGE,"E18.filletArc"),sQuery(id+"F0.wireOp",EDGE,"E19.filletArc"),sQuery(id+"F0.wireOp",EDGE,"E20.filletArc"),sQuery(id+"F0.wireOp",EDGE,"E25.0"),sQuery(id+"F0.wireOp",EDGE,"E25.1"),sQuery(id+"F0.wireOp",EDGE,"E25.2"),sQuery(id+"F0.wireOp",EDGE,"E25.3"),sQuery(id+"F0.wireOp",EDGE,"E25.4"),sQuery(id+"F0.wireOp",EDGE,"E25.5"),sQuery(id+"F0.wireOp",EDGE,"E25.6"),sQuery(id+"F0.wireOp",EDGE,"E25.7")])],"isStart":false});
            extrude(context, id + "F17", {"entities" : qUnion([Q0, Q1, Q2]), "endBound" : BoundingType.UP_TO_SURFACE, "endBoundEntityFace" : qUnion([Q3]), "depth" : 25 * mm});
        }
    });
